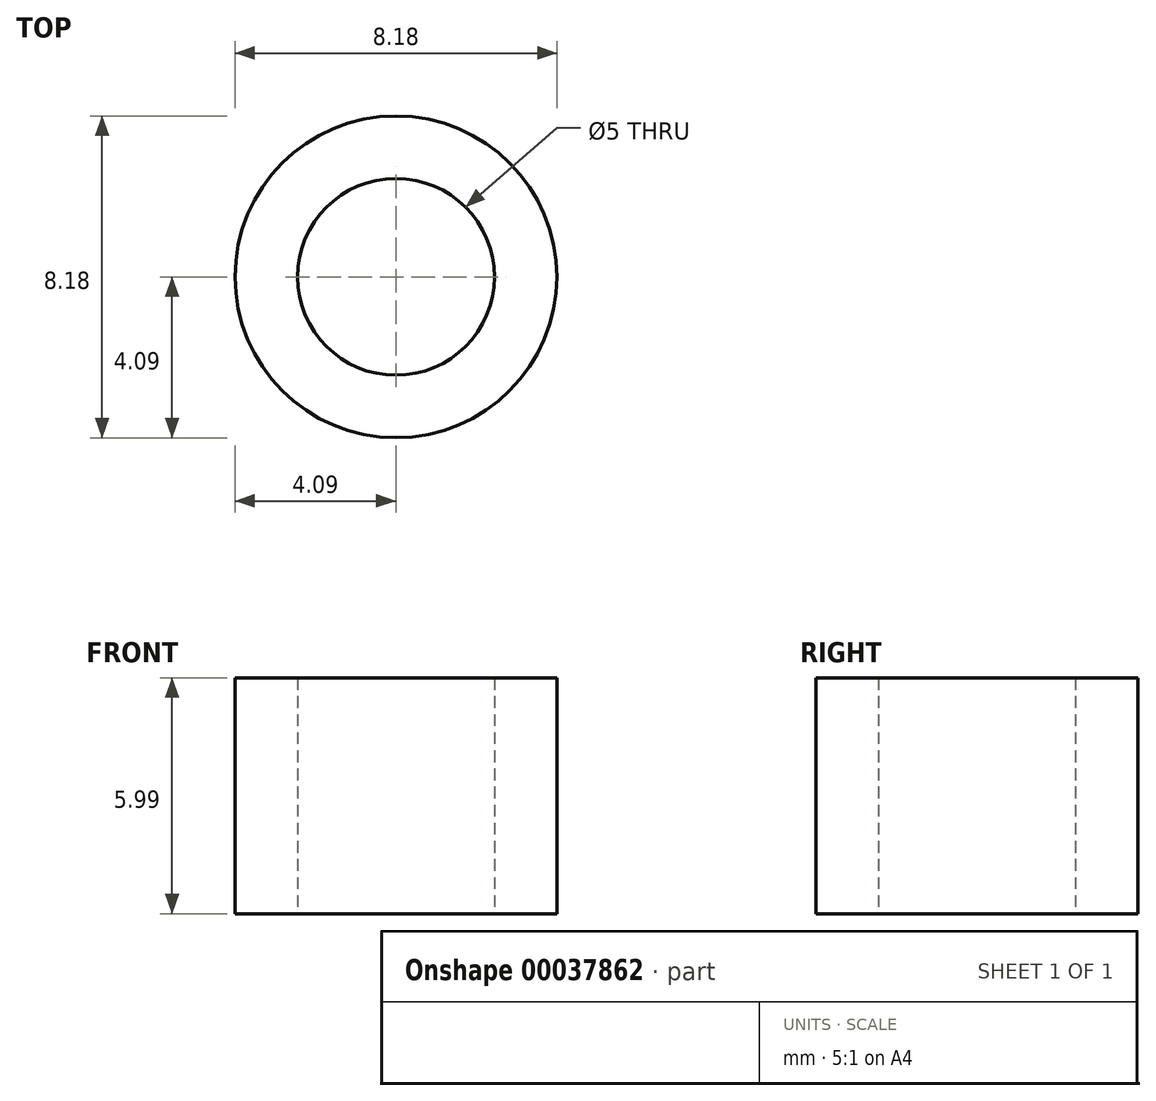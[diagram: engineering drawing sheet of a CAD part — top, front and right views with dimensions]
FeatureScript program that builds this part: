
annotation { "Feature Type Name" : "Feature", "Feature Type Description" : "" }
export const myFeature = defineFeature(function(context is Context, id is Id, definition is map)
    precondition{}
    {
        {
            var Q0;
            Q0=qCreatedBy(makeId("Top.planeOp"),FACE);
            var sketch = newSketch(context, id + "F0", { "sketchPlane" : qUnion([Q0])});
            skCircle(sketch, "E0", {"center": v(0, 0) * mm, "radius": 4.09 * mm});
            skCircle(sketch, "E1", {"center": v(0, 0) * mm, "radius": 2.5 * mm});
            skSolve(sketch);
        }
        {
            var Q0;
            Q0 = qSketchRegion(id + "F0", true);
            extrude(context, id + "F1", {"entities" : qUnion([Q0]), "depth" : 6 * mm});
        }
    });
